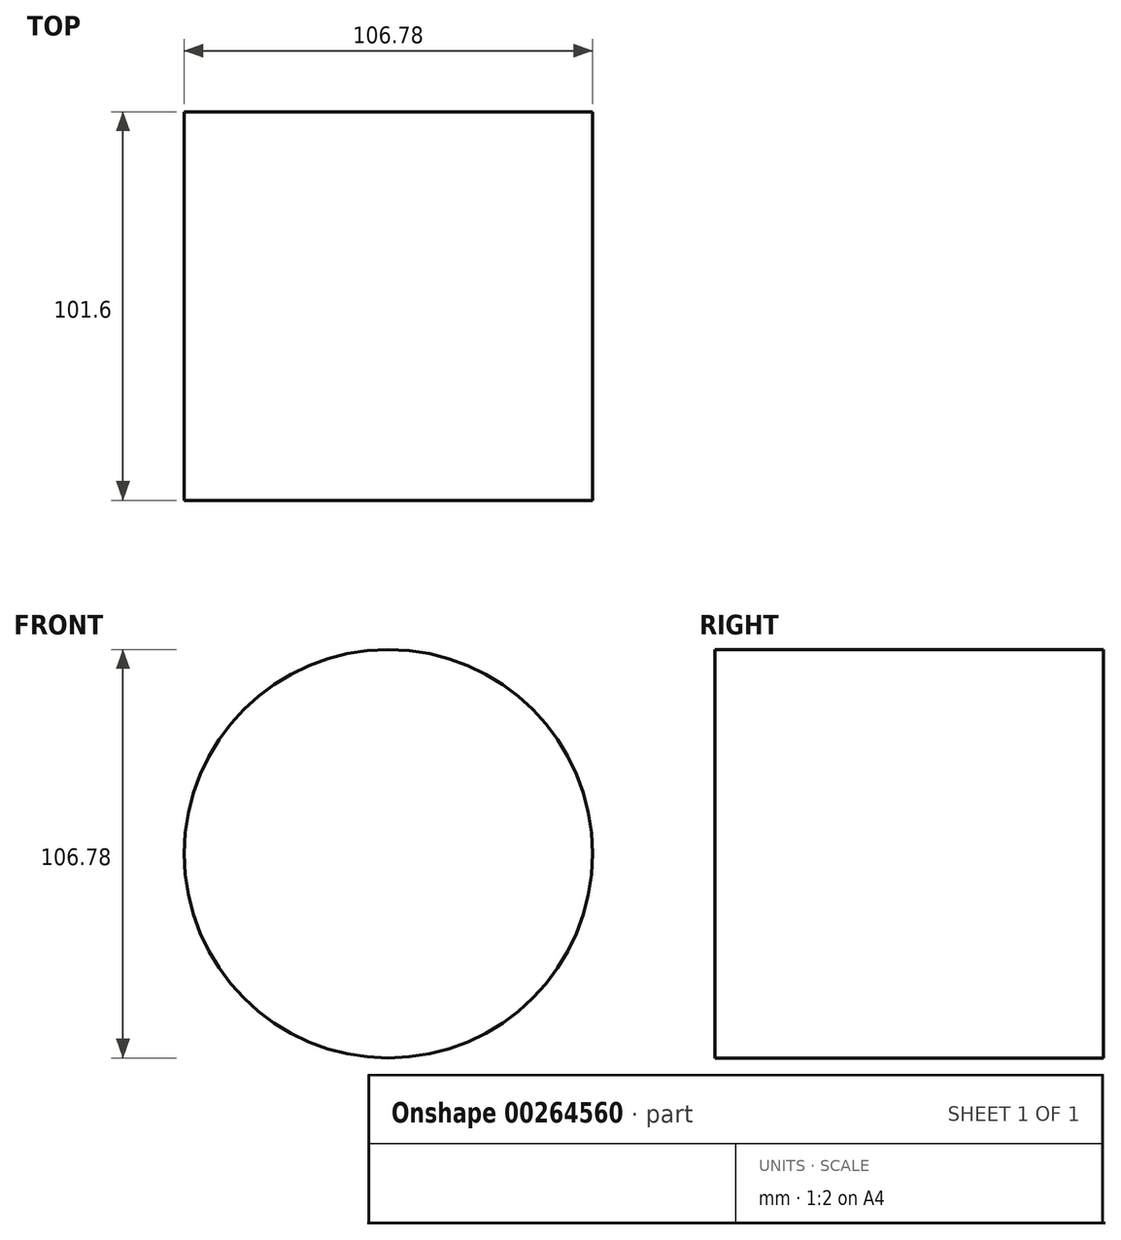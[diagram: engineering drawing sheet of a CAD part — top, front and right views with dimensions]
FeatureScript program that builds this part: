
annotation { "Feature Type Name" : "Feature", "Feature Type Description" : "" }
export const myFeature = defineFeature(function(context is Context, id is Id, definition is map)
    precondition{}
    {
        {
            var Q0;
            Q0=qCreatedBy(makeId("Front.planeOp"),FACE);
            var sketch = newSketch(context, id + "F0", { "sketchPlane" : qUnion([Q0])});
            skCircle(sketch, "E0", {"center": v(0, 0) * mm, "radius": 53.39 * mm});
            skSolve(sketch);
        }
        {
            var Q0;
            Q0=makeQuery(id+"F0.imprint","IMPRINT",FACE,{"disambiguationData":[TD([[makeQuery(id+"F0.imprint","IMPRINT",EDGE,{"derivedFrom":sQuery(id+"F0.wireOp",EDGE,"E0")}),1.0]])]});
            extrude(context, id + "F1", {"entities" : qUnion([Q0]), "depth" : 101.6 * mm});
        }
    });
